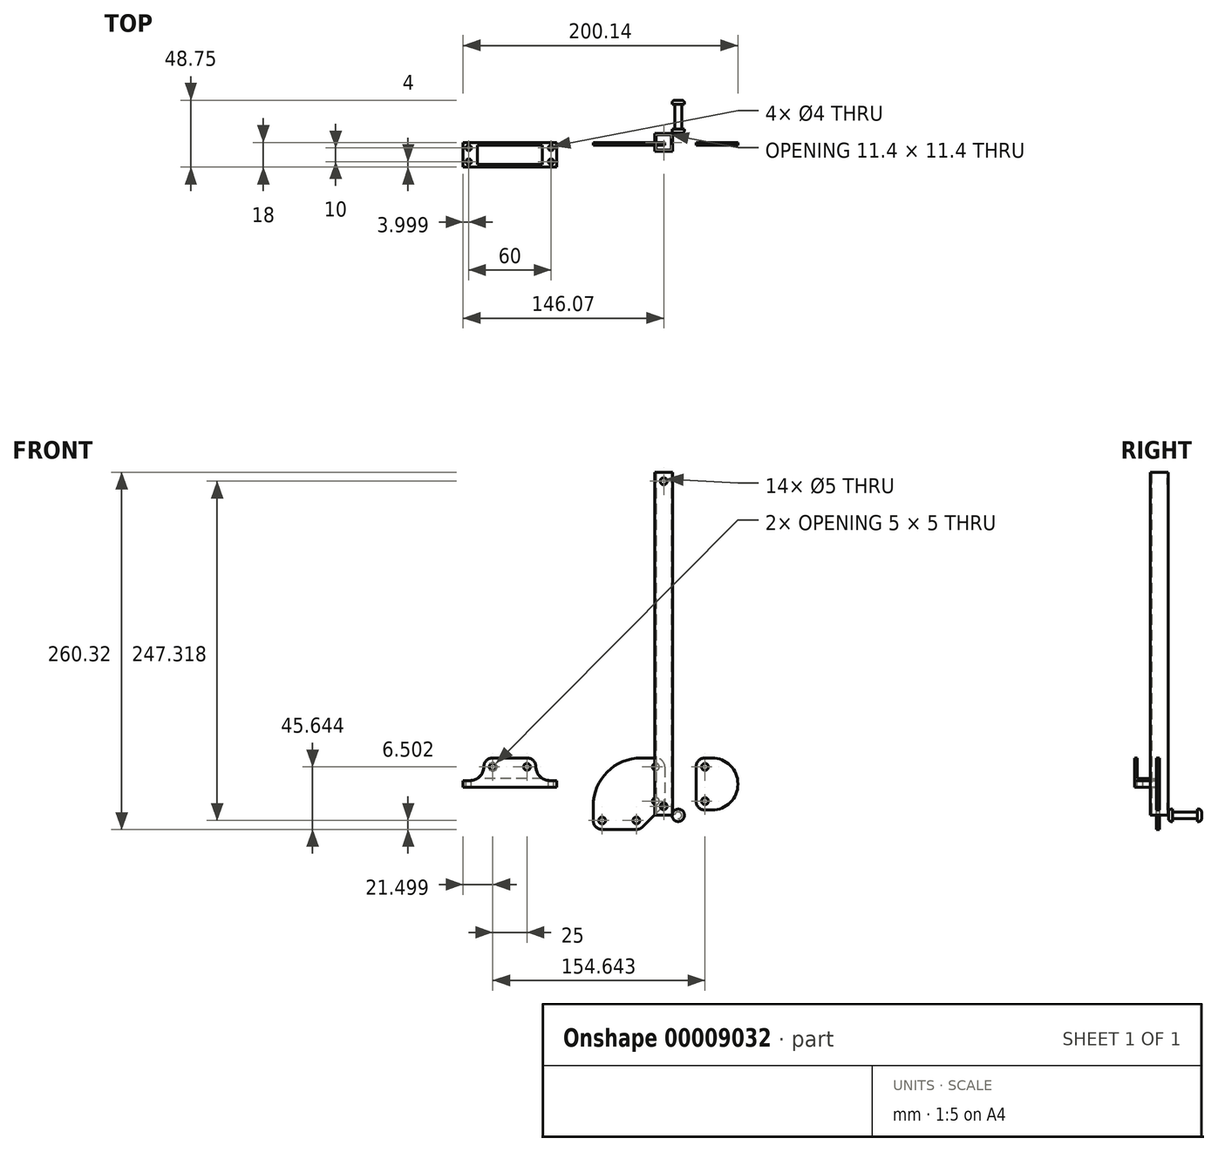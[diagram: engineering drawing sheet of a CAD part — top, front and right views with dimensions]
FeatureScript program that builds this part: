
annotation { "Feature Type Name" : "Feature", "Feature Type Description" : "" }
export const myFeature = defineFeature(function(context is Context, id is Id, definition is map)
    precondition{}
    {
        {
            var Q0;
            Q0=qCreatedBy(makeId("Top.planeOp"),FACE);
            var sketch = newSketch(context, id + "F0", { "sketchPlane" : qUnion([Q0])});
            skLineSegment(sketch, "E0.rect.bottom", {"start": v(6.5, -6.5) * mm, "end": v(-6.5, -6.5) * mm});
            skLineSegment(sketch, "E0.rect.top", {"start": v(6.5, 6.5) * mm, "end": v(-6.5, 6.5) * mm});
            skLineSegment(sketch, "E0.rect.left", {"start": v(6.5, -6.5) * mm, "end": v(6.5, 6.5) * mm});
            skLineSegment(sketch, "E0.rect.right", {"start": v(-6.5, -6.5) * mm, "end": v(-6.5, 6.5) * mm});
            skPoint(sketch, "E0.rect.middle", {"position": v(0, 0) * mm});
            skLineSegment(sketch, "E1.0", {"start": v(4.9, 5.7) * mm, "end": v(-4.9, 5.7) * mm});
            skLineSegment(sketch, "E1.1", {"start": v(5.7, -4.9) * mm, "end": v(5.7, 4.9) * mm});
            skLineSegment(sketch, "E1.2", {"start": v(4.9, -5.7) * mm, "end": v(-4.9, -5.7) * mm});
            skLineSegment(sketch, "E1.3", {"start": v(-5.7, -4.9) * mm, "end": v(-5.7, 4.9) * mm});
            skPoint(sketch, "E2.visualSharp", {"position": v(-5.7, 5.7) * mm});
            skArc(sketch, "E2.filletArc", {"start": v(-4.9, 5.7) * mm, "mid": v(-5.47, 5.47) * mm, "end": v(-5.7, 4.9) * mm});
            skPoint(sketch, "E3.visualSharp", {"position": v(5.7, 5.7) * mm});
            skArc(sketch, "E3.filletArc", {"start": v(5.7, 4.9) * mm, "mid": v(5.47, 5.47) * mm, "end": v(4.9, 5.7) * mm});
            skPoint(sketch, "E4.visualSharp", {"position": v(5.7, -5.7) * mm});
            skArc(sketch, "E4.filletArc", {"start": v(4.9, -5.7) * mm, "mid": v(5.47, -5.47) * mm, "end": v(5.7, -4.9) * mm});
            skPoint(sketch, "E5.visualSharp", {"position": v(-5.7, -5.7) * mm});
            skArc(sketch, "E5.filletArc", {"start": v(-5.7, -4.9) * mm, "mid": v(-5.47, -5.47) * mm, "end": v(-4.9, -5.7) * mm});
            skSolve(sketch);
        }
        {
            var Q0;
            Q0=makeQuery(id+"F0.imprint","IMPRINT",FACE,{"disambiguationData":[TD([[makeQuery(id+"F0.imprint","IMPRINT",EDGE,{"derivedFrom":sQuery(id+"F0.wireOp",EDGE,"E0.rect.bottom")}),-1.0]])]});
            extrude(context, id + "F1", {"entities" : qUnion([Q0]), "depth" : 250 * mm});
        }
        {
            var Q0;
            Q0=makeQuery(id+"F1.opExtrude","SWEPT_FACE",FACE,{"disambiguationData":[OSD([sQuery(id+"F0.wireOp",EDGE,"E0.rect.bottom")])]});
            var sketch = newSketch(context, id + "F2", { "sketchPlane" : qUnion([Q0])});
            skLineSegment(sketch, "E6.0.0", {"start": v(-6.5, 0) * mm, "end": v(6.5, 0) * mm});
            skLineSegment(sketch, "E6.0.1", {"start": v(6.5, 0) * mm, "end": v(6.5, 250) * mm});
            skLineSegment(sketch, "E6.0.2", {"start": v(6.5, 250) * mm, "end": v(-6.5, 250) * mm});
            skLineSegment(sketch, "E6.0.3", {"start": v(-6.5, 250) * mm, "end": v(-6.5, 0) * mm});
            skCircle(sketch, "E7", {"center": v(0, 6.5) * mm, "radius": 2.5 * mm});
            skCircle(sketch, "E8", {"center": v(0, 243.5) * mm, "radius": 2.5 * mm});
            skLineSegment(sketch, "E9", {"start": v(0, 6.5) * mm, "end": v(0, 0) * mm});
            skLineSegment(sketch, "E10", {"start": v(0, 250) * mm, "end": v(0, 243.5) * mm});
            skSolve(sketch);
        }
        {
            var Q0;
            Q0=makeQuery(id+"F2.imprint","IMPRINT",FACE,{"disambiguationData":[TD([[makeQuery(id+"F2.imprint","IMPRINT",EDGE,{"derivedFrom":sQuery(id+"F2.wireOp",EDGE,"E7")}),1.0]])]});
            var Q1;
            Q1=makeQuery(id+"F2.imprint","IMPRINT",FACE,{"disambiguationData":[TD([[makeQuery(id+"F2.imprint","IMPRINT",EDGE,{"derivedFrom":sQuery(id+"F2.wireOp",EDGE,"E8")}),1.0]])]});
            extrude(context, id + "F3", {"entities" : qUnion([Q0, Q1]), "operationType" : NewBodyOperationType.REMOVE, "oppositeDirection" : true, "depth" : 15 * mm});
        }
        {
            var Q0;
            Q0=qCreatedBy(makeId("Front.planeOp"),FACE);
            var sketch = newSketch(context, id + "F4", { "sketchPlane" : qUnion([Q0])});
            skCircle(sketch, "E11", {"center": v(-5.72, 35.32) * mm, "radius": 2.5 * mm});
            skCircle(sketch, "E12", {"center": v(-5.72, 10.32) * mm, "radius": 2.5 * mm});
            skCircle(sketch, "E13", {"center": v(-19.87, -3.82) * mm, "radius": 2.5 * mm});
            skCircle(sketch, "E14", {"center": v(-44.87, -3.82) * mm, "radius": 2.5 * mm});
            skLineSegment(sketch, "E15", {"start": v(-5.72, 35.32) * mm, "end": v(-5.72, 10.32) * mm, "construction": true});
            skLineSegment(sketch, "E16", {"start": v(-44.87, -3.82) * mm, "end": v(-19.87, -3.82) * mm, "construction": true});
            skCircle(sketch, "E17", {"center": v(-5.72, -3.82) * mm, "radius": 14.14 * mm, "construction": true});
            skArc(sketch, "E18", {"start": v(0.78, 35.32) * mm, "mid": v(-1.13, 39.92) * mm, "end": v(-5.72, 41.82) * mm});
            skArc(sketch, "E19", {"start": v(-1.13, 5.73) * mm, "mid": v(0.28, 7.84) * mm, "end": v(0.78, 10.32) * mm});
            skArc(sketch, "E20", {"start": v(-19.87, -10.32) * mm, "mid": v(-17.38, -9.82) * mm, "end": v(-15.27, -8.41) * mm});
            skArc(sketch, "E21", {"start": v(-51.37, -3.82) * mm, "mid": v(-49.46, -8.41) * mm, "end": v(-44.87, -10.32) * mm});
            skLineSegment(sketch, "E22", {"start": v(0.78, 35.32) * mm, "end": v(0.78, 10.32) * mm});
            skLineSegment(sketch, "E23", {"start": v(-1.13, 5.73) * mm, "end": v(-15.27, -8.41) * mm});
            skLineSegment(sketch, "E24", {"start": v(-44.87, -10.32) * mm, "end": v(-19.87, -10.32) * mm});
            skLineSegment(sketch, "E25", {"start": v(-51.37, -3.82) * mm, "end": v(-51.37, 6.82) * mm});
            skLineSegment(sketch, "E26", {"start": v(-16.37, 41.82) * mm, "end": v(-5.72, 41.82) * mm});
            skPoint(sketch, "E27.visualSharp", {"position": v(-51.37, 41.82) * mm});
            skArc(sketch, "E27.filletArc", {"start": v(-16.37, 41.82) * mm, "mid": v(-41.11, 31.57) * mm, "end": v(-51.37, 6.82) * mm});
            skLineSegment(sketch, "E28", {"start": v(30.07, 35.32) * mm, "end": v(30.07, 10.32) * mm, "construction": true});
            skCircle(sketch, "E29", {"center": v(30.07, 35.32) * mm, "radius": 2.5 * mm});
            skCircle(sketch, "E30", {"center": v(30.07, 10.32) * mm, "radius": 2.5 * mm});
            skArc(sketch, "E31", {"start": v(30.07, 41.82) * mm, "mid": v(25.48, 39.92) * mm, "end": v(23.57, 35.32) * mm});
            skArc(sketch, "E32", {"start": v(23.57, 10.32) * mm, "mid": v(25.48, 5.73) * mm, "end": v(30.07, 3.82) * mm});
            skLineSegment(sketch, "E33", {"start": v(23.57, 35.32) * mm, "end": v(23.57, 10.32) * mm});
            skLineSegment(sketch, "E34", {"start": v(30.07, 41.82) * mm, "end": v(35.07, 41.82) * mm});
            skLineSegment(sketch, "E35", {"start": v(30.07, 3.82) * mm, "end": v(35.07, 3.82) * mm});
            skArc(sketch, "E36", {"start": v(35.07, 3.82) * mm, "mid": v(54.07, 22.82) * mm, "end": v(35.07, 41.82) * mm});
            skLineSegment(sketch, "E37", {"start": v(-124.57, 35.32) * mm, "end": v(-99.57, 35.32) * mm, "construction": true});
            skArc(sketch, "E38", {"start": v(-124.57, 41.82) * mm, "mid": v(-129.17, 39.92) * mm, "end": v(-131.07, 35.32) * mm});
            skArc(sketch, "E39", {"start": v(-93.07, 35.32) * mm, "mid": v(-94.97, 39.92) * mm, "end": v(-99.57, 41.82) * mm});
            skCircle(sketch, "E40", {"center": v(-99.57, 35.32) * mm, "radius": 2.5 * mm});
            skCircle(sketch, "E41", {"center": v(-124.57, 35.32) * mm, "radius": 2.5 * mm});
            skLineSegment(sketch, "E42", {"start": v(-124.57, 41.82) * mm, "end": v(-99.57, 41.82) * mm});
            skLineSegment(sketch, "E43", {"start": v(-131.07, 35.32) * mm, "end": v(-131.07, 25.32) * mm, "construction": true});
            skLineSegment(sketch, "E44", {"start": v(-131.07, 25.32) * mm, "end": v(-141.07, 25.32) * mm, "construction": true});
            skArc(sketch, "E45", {"start": v(-141.07, 25.32) * mm, "mid": v(-134, 28.25) * mm, "end": v(-131.07, 35.32) * mm});
            skLineSegment(sketch, "E46", {"start": v(-93.07, 35.32) * mm, "end": v(-93.07, 25.32) * mm, "construction": true});
            skLineSegment(sketch, "E47", {"start": v(-93.07, 25.32) * mm, "end": v(-83.07, 25.32) * mm, "construction": true});
            skArc(sketch, "E48", {"start": v(-93.07, 35.32) * mm, "mid": v(-90.14, 28.25) * mm, "end": v(-83.07, 25.32) * mm});
            skLineSegment(sketch, "E49", {"start": v(-141.07, 25.32) * mm, "end": v(-146.07, 25.32) * mm});
            skLineSegment(sketch, "E50", {"start": v(-146.07, 25.32) * mm, "end": v(-146.07, 20.32) * mm});
            skLineSegment(sketch, "E51", {"start": v(-146.07, 20.32) * mm, "end": v(-78.07, 20.32) * mm});
            skLineSegment(sketch, "E52", {"start": v(-78.07, 20.32) * mm, "end": v(-78.07, 25.32) * mm});
            skLineSegment(sketch, "E53", {"start": v(-78.07, 25.32) * mm, "end": v(-83.07, 25.32) * mm});
            skLineSegment(sketch, "E54", {"start": v(-141.07, 25.32) * mm, "end": v(-83.07, 25.32) * mm});
            skSolve(sketch);
        }
        {
            var Q0;
            Q0=makeQuery(id+"F4.imprint","IMPRINT",FACE,{"disambiguationData":[TD([[makeQuery(id+"F4.imprint","IMPRINT",EDGE,{"derivedFrom":sQuery(id+"F4.wireOp",EDGE,"E29")}),-1.0]])]});
            var Q1;
            Q1=makeQuery(id+"F4.imprint","IMPRINT",FACE,{"disambiguationData":[TD([[makeQuery(id+"F4.imprint","IMPRINT",EDGE,{"derivedFrom":sQuery(id+"F4.wireOp",EDGE,"E11")}),-1.0]])]});
            extrude(context, id + "F5", {"entities" : qUnion([Q0, Q1]), "depth" : 2 * mm});
        }
        {
            var Q0;
            Q0=makeQuery(id+"F4.imprint","IMPRINT",FACE,{"disambiguationData":[TD([[makeQuery(id+"F4.imprint","IMPRINT",EDGE,{"derivedFrom":sQuery(id+"F4.wireOp",EDGE,"E38")}),1.0]])]});
            var Q1;
            Q1=makeQuery(id+"F4.imprint","IMPRINT",FACE,{"disambiguationData":[TD([[makeQuery(id+"F4.imprint","IMPRINT",EDGE,{"derivedFrom":sQuery(id+"F4.wireOp",EDGE,"E49")}),1.0]])]});
            extrude(context, id + "F6", {"entities" : qUnion([Q0, Q1]), "depth" : 18 * mm});
        }
        {
            var Q0;
            Q0=makeQuery(id+"F6.opExtrude","SWEPT_FACE",FACE,{"disambiguationData":[OSD([sQuery(id+"F4.wireOp",EDGE,"E42")])]});
            var sketch = newSketch(context, id + "F7", { "sketchPlane" : qUnion([Q0])});
            skLineSegment(sketch, "E55.0.0", {"start": v(-99.57, 0) * mm, "end": v(-124.57, 0) * mm});
            skLineSegment(sketch, "E55.0.1", {"start": v(-124.57, 0) * mm, "end": v(-124.57, -18) * mm});
            skLineSegment(sketch, "E55.0.2", {"start": v(-124.57, -18) * mm, "end": v(-99.57, -18) * mm});
            skLineSegment(sketch, "E55.0.3", {"start": v(-99.57, -18) * mm, "end": v(-99.57, 0) * mm});
            skLineSegment(sketch, "E56", {"start": v(-112.07, 0) * mm, "end": v(-112.07, -18) * mm});
            skLineSegment(sketch, "E57.rect.bottom", {"start": v(-62.07, -16) * mm, "end": v(-162.07, -16) * mm});
            skLineSegment(sketch, "E57.rect.top", {"start": v(-62.07, -2) * mm, "end": v(-162.07, -2) * mm});
            skLineSegment(sketch, "E57.rect.left", {"start": v(-62.07, -16) * mm, "end": v(-62.07, -2) * mm});
            skLineSegment(sketch, "E57.rect.right", {"start": v(-162.07, -16) * mm, "end": v(-162.07, -2) * mm});
            skPoint(sketch, "E57.rect.middle", {"position": v(-112.07, -9) * mm});
            skSolve(sketch);
        }
        {
            var Q0;
            {var subQ0=sQuery(id+"F7.wireOp",EDGE,"E57.rect.left");Q0=makeQuery(id+"F7.imprint","IMPRINT",FACE,{"disambiguationData":[TD([[makeQuery(id+"F7.imprint","IMPRINT",EDGE,{"derivedFrom":subQ0}),1.0]])]});}
            var Q1;
            {var subQ0=sQuery(id+"F7.wireOp",EDGE,"E57.rect.bottom");var subQ3=sQuery(id+"F7.wireOp",EDGE,"E55.0.3");var subQ4=makeQuery(id+"F7.imprint","INTERSECT",VERTEX,{"derivedFrom":[subQ3,subQ0]});Q1=makeQuery(id+"F7.imprint","IMPRINT",FACE,{"disambiguationData":[TD([[makeQuery(id+"F7.imprint","IMPRINT",EDGE,{"disambiguationData":[TD([[subQ4,-1.0]])],"derivedFrom":subQ3}),1.0]])]});}
            var Q2;
            {var subQ3=sQuery(id+"F7.wireOp",EDGE,"E55.0.1");var subQ5=sQuery(id+"F7.wireOp",EDGE,"E57.rect.bottom");var subQ7=makeQuery(id+"F7.imprint","INTERSECT",VERTEX,{"derivedFrom":[subQ3,subQ5]});Q2=makeQuery(id+"F7.imprint","IMPRINT",FACE,{"disambiguationData":[TD([[makeQuery(id+"F7.imprint","IMPRINT",EDGE,{"disambiguationData":[TD([[subQ7,-1.0]])],"derivedFrom":subQ3}),-1.0]])]});}
            var Q3;
            {var subQ0=sQuery(id+"F7.wireOp",EDGE,"E57.rect.right");Q3=makeQuery(id+"F7.imprint","IMPRINT",FACE,{"disambiguationData":[TD([[makeQuery(id+"F7.imprint","IMPRINT",EDGE,{"derivedFrom":subQ0}),-1.0]])]});}
            extrude(context, id + "F8", {"entities" : qUnion([Q0, Q1, Q2, Q3]), "operationType" : NewBodyOperationType.REMOVE, "oppositeDirection" : true, "depth" : 15 * mm});
        }
        {
            var Q0;
            Q0=qCreatedBy(makeId("Top.planeOp"),FACE);
            var sketch = newSketch(context, id + "F9", { "sketchPlane" : qUnion([Q0])});
            skLineSegment(sketch, "E58", {"start": v(13.1, 27.75) * mm, "end": v(13.1, 9.75) * mm});
            skLineSegment(sketch, "E59", {"start": v(13.1, 9.75) * mm, "end": v(15.1, 9.75) * mm});
            skLineSegment(sketch, "E60", {"start": v(15.1, 9.75) * mm, "end": v(15.1, 8.75) * mm});
            skLineSegment(sketch, "E61", {"start": v(13.1, 6.75) * mm, "end": v(10.6, 6.75) * mm});
            skLineSegment(sketch, "E62", {"start": v(13.1, 27.75) * mm, "end": v(15.1, 27.75) * mm});
            skLineSegment(sketch, "E63", {"start": v(15.1, 27.75) * mm, "end": v(15.1, 28.75) * mm});
            skLineSegment(sketch, "E64", {"start": v(13.1, 30.75) * mm, "end": v(10.6, 30.75) * mm});
            skLineSegment(sketch, "E65", {"start": v(10.6, 30.75) * mm, "end": v(10.6, 6.75) * mm});
            skLineSegment(sketch, "E66", {"start": v(10.6, 18.75) * mm, "end": v(13.1, 18.75) * mm, "construction": true});
            skPoint(sketch, "E67.visualSharp", {"position": v(15.1, 6.75) * mm});
            skArc(sketch, "E67.filletArc", {"start": v(13.1, 6.75) * mm, "mid": v(14.51, 7.34) * mm, "end": v(15.1, 8.75) * mm});
            skPoint(sketch, "E68.visualSharp", {"position": v(15.1, 30.75) * mm});
            skArc(sketch, "E68.filletArc", {"start": v(15.1, 28.75) * mm, "mid": v(14.51, 30.16) * mm, "end": v(13.1, 30.75) * mm});
            skSolve(sketch);
        }
        {
            var Q0;
            Q0=makeQuery(id+"F9.imprint","IMPRINT",FACE,{"disambiguationData":[TD([[makeQuery(id+"F9.imprint","IMPRINT",EDGE,{"derivedFrom":sQuery(id+"F9.wireOp",EDGE,"E58")}),-1.0]])]});
            var Q1;
            Q1=sQuery(id+"F9.wireOp",EDGE,"E65");
            revolve(context, id + "F10", {"entities" : qUnion([Q0]), "axis" : qUnion([Q1]), "revolveType" : RevolveType.FULL});
        }
        {
            var Q0;
            Q0=makeQuery(id+"F8.boolean.opBoolean","COPY",FACE,{"derivedFrom":makeQuery(id+"F8.opExtrude","CAP_FACE",FACE,{"disambiguationData":[OSD([sQuery(id+"F7.wireOp",EDGE,"E57.rect.bottom"),sQuery(id+"F7.wireOp",EDGE,"E57.rect.top"),sQuery(id+"F7.wireOp",EDGE,"E57.rect.left"),sQuery(id+"F7.wireOp",EDGE,"E57.rect.right")])],"isStart":false})});
            var sketch = newSketch(context, id + "F11", { "sketchPlane" : qUnion([Q0])});
            skLineSegment(sketch, "E69.0.0", {"start": v(-146.07, 0) * mm, "end": v(-78.07, 0) * mm});
            skLineSegment(sketch, "E69.0.1", {"start": v(-78.07, 0) * mm, "end": v(-78.07, -18) * mm});
            skLineSegment(sketch, "E69.0.2", {"start": v(-78.07, -18) * mm, "end": v(-146.07, -18) * mm});
            skLineSegment(sketch, "E69.0.3", {"start": v(-146.07, -18) * mm, "end": v(-146.07, 0) * mm});
            skLineSegment(sketch, "E70", {"start": v(-142.07, 0) * mm, "end": v(-142.07, -4) * mm, "construction": true});
            skLineSegment(sketch, "E71", {"start": v(-142.07, -4) * mm, "end": v(-146.07, -4) * mm, "construction": true});
            skCircle(sketch, "E72", {"center": v(-142.07, -4) * mm, "radius": 2 * mm});
            skCircle(sketch, "E73", {"center": v(-142.07, -14) * mm, "radius": 2 * mm});
            skCircle(sketch, "E74", {"center": v(-82.07, -14) * mm, "radius": 2 * mm});
            skCircle(sketch, "E75", {"center": v(-82.07, -4) * mm, "radius": 2 * mm});
            skLineSegment(sketch, "E76", {"start": v(-142.07, -14) * mm, "end": v(-142.07, -18) * mm, "construction": true});
            skLineSegment(sketch, "E77", {"start": v(-82.07, -4) * mm, "end": v(-78.07, -4) * mm, "construction": true});
            skSolve(sketch);
        }
        {
            var Q0;
            Q0=makeQuery(id+"F11.imprint","IMPRINT",FACE,{"disambiguationData":[TD([[makeQuery(id+"F11.imprint","IMPRINT",EDGE,{"derivedFrom":sQuery(id+"F11.wireOp",EDGE,"E73")}),1.0]])]});
            var Q1;
            Q1=makeQuery(id+"F11.imprint","IMPRINT",FACE,{"disambiguationData":[TD([[makeQuery(id+"F11.imprint","IMPRINT",EDGE,{"derivedFrom":sQuery(id+"F11.wireOp",EDGE,"E72")}),1.0]])]});
            var Q2;
            Q2=makeQuery(id+"F11.imprint","IMPRINT",FACE,{"disambiguationData":[TD([[makeQuery(id+"F11.imprint","IMPRINT",EDGE,{"derivedFrom":sQuery(id+"F11.wireOp",EDGE,"E75")}),1.0]])]});
            var Q3;
            Q3=makeQuery(id+"F11.imprint","IMPRINT",FACE,{"disambiguationData":[TD([[makeQuery(id+"F11.imprint","IMPRINT",EDGE,{"derivedFrom":sQuery(id+"F11.wireOp",EDGE,"E74")}),1.0]])]});
            extrude(context, id + "F12", {"entities" : qUnion([Q0, Q1, Q2, Q3]), "operationType" : NewBodyOperationType.REMOVE, "oppositeDirection" : true, "depth" : 10 * mm});
        }
    });
